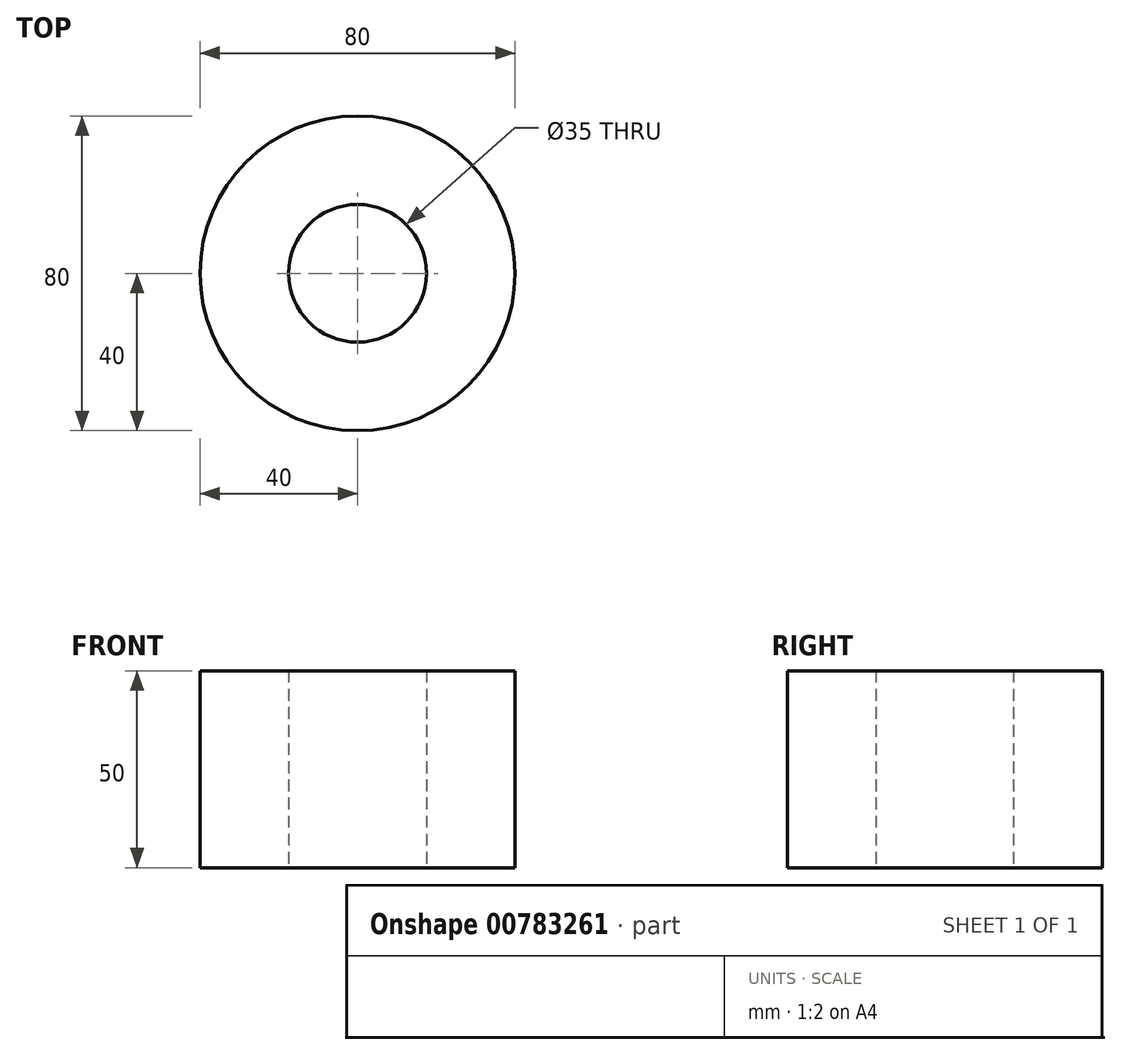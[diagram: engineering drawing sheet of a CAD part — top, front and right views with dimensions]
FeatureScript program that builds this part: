
annotation { "Feature Type Name" : "Feature", "Feature Type Description" : "" }
export const myFeature = defineFeature(function(context is Context, id is Id, definition is map)
    precondition{}
    {
        {
            var Q0;
            Q0=qCreatedBy(makeId("Top.planeOp"),FACE);
            var sketch = newSketch(context, id + "F0", { "sketchPlane" : qUnion([Q0])});
            skCircle(sketch, "E0", {"center": v(0, 0) * mm, "radius": 40 * mm});
            skCircle(sketch, "E1", {"center": v(0, 0) * mm, "radius": 17.5 * mm});
            skSolve(sketch);
        }
        {
            var Q0;
            Q0=makeQuery(id+"F0.imprint","IMPRINT",FACE,{"disambiguationData":[TD([[makeQuery(id+"F0.imprint","IMPRINT",EDGE,{"derivedFrom":sQuery(id+"F0.wireOp",EDGE,"E0")}),1.0]])]});
            extrude(context, id + "F1", {"entities" : qUnion([Q0]), "depth" : 50 * mm, "offsetDistance" : 25 * mm});
        }
    });
